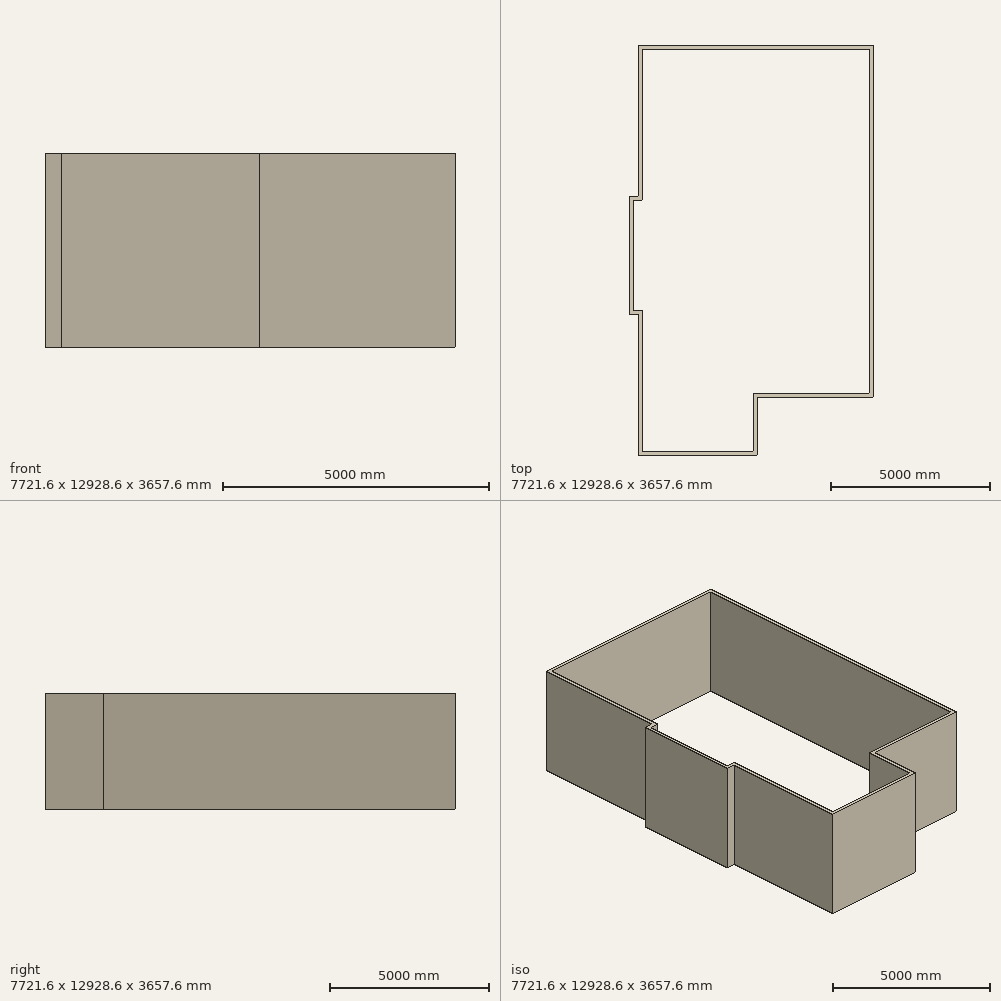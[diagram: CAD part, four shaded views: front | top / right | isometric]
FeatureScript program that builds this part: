
annotation { "Feature Type Name" : "Feature", "Feature Type Description" : "" }
export const myFeature = defineFeature(function(context is Context, id is Id, definition is map)
    precondition{}
    {
        {
            var Q0;
            Q0=qCreatedBy(makeId("Top.planeOp"),FACE);
            var sketch = newSketch(context, id + "F0", { "sketchPlane" : qUnion([Q0])});
            skLineSegment(sketch, "E0", {"start": v(3683, 0) * mm, "end": v(3683, 11099.8) * mm});
            skLineSegment(sketch, "E1", {"start": v(3683, 11099.8) * mm, "end": v(-3733.8, 11099.8) * mm});
            skLineSegment(sketch, "E2", {"start": v(-3733.8, 11099.8) * mm, "end": v(-3733.8, 6324.6) * mm});
            skLineSegment(sketch, "E3", {"start": v(-3733.8, 6324.6) * mm, "end": v(-4038.6, 6324.6) * mm});
            skLineSegment(sketch, "E4", {"start": v(-4038.6, 6324.6) * mm, "end": v(-4038.6, 2616.2) * mm});
            skLineSegment(sketch, "E5", {"start": v(-4038.6, 2616.2) * mm, "end": v(-3733.8, 2616.2) * mm});
            skLineSegment(sketch, "E6", {"start": v(-3733.8, 2616.2) * mm, "end": v(-3733.8, -1828.8) * mm});
            skLineSegment(sketch, "E7", {"start": v(0, -1828.8) * mm, "end": v(0, 0) * mm});
            skLineSegment(sketch, "E8", {"start": v(0, 0) * mm, "end": v(3683, 0) * mm});
            skPoint(sketch, "E9.orphan", {"position": v(3683, 0) * mm});
            skLineSegment(sketch, "E10", {"start": v(-3733.8, -1828.8) * mm, "end": v(0, -1828.8) * mm});
            skLineSegment(sketch, "E11.0", {"start": v(-127, -1701.8) * mm, "end": v(-127, 127) * mm});
            skLineSegment(sketch, "E11.1", {"start": v(-3606.8, -1701.8) * mm, "end": v(-127, -1701.8) * mm});
            skLineSegment(sketch, "E11.2", {"start": v(-3606.8, 2743.2) * mm, "end": v(-3606.8, -1701.8) * mm});
            skLineSegment(sketch, "E11.3", {"start": v(-3911.6, 2743.2) * mm, "end": v(-3606.8, 2743.2) * mm});
            skLineSegment(sketch, "E11.4", {"start": v(-3911.6, 6197.6) * mm, "end": v(-3911.6, 2743.2) * mm});
            skLineSegment(sketch, "E11.5", {"start": v(-127, 127) * mm, "end": v(3556, 127) * mm});
            skLineSegment(sketch, "E11.6", {"start": v(-3606.8, 6197.6) * mm, "end": v(-3911.6, 6197.6) * mm});
            skLineSegment(sketch, "E11.7", {"start": v(-3606.8, 10972.8) * mm, "end": v(-3606.8, 6197.6) * mm});
            skLineSegment(sketch, "E11.8", {"start": v(3556, 10972.8) * mm, "end": v(-3606.8, 10972.8) * mm});
            skLineSegment(sketch, "E11.9", {"start": v(3556, 127) * mm, "end": v(3556, 10972.8) * mm});
            skLineSegment(sketch, "E12.bottom", {"start": v(-3746.5, 438.15) * mm, "end": v(-3594.1, 438.15) * mm, "construction": true});
            skLineSegment(sketch, "E12.top", {"start": v(-3746.5, 1352.55) * mm, "end": v(-3594.1, 1352.55) * mm, "construction": true});
            skLineSegment(sketch, "E12.left", {"start": v(-3746.5, 438.15) * mm, "end": v(-3746.5, 1352.55) * mm, "construction": true});
            skLineSegment(sketch, "E12.right", {"start": v(-3594.1, 438.15) * mm, "end": v(-3594.1, 1352.55) * mm, "construction": true});
            skLineSegment(sketch, "E13", {"start": v(-3606.8, 2609.85) * mm, "end": v(-2933.7, 2609.85) * mm, "construction": true});
            skLineSegment(sketch, "E14", {"start": v(-2933.7, 2609.85) * mm, "end": v(-2933.7, 2743.2) * mm, "construction": true});
            skLineSegment(sketch, "E15", {"start": v(-2933.7, 2743.2) * mm, "end": v(-3606.8, 2743.2) * mm, "construction": true});
            skLineSegment(sketch, "E16.bottom", {"start": v(-2705.1, -1689.1) * mm, "end": v(-1054.1, -1689.1) * mm, "construction": true});
            skLineSegment(sketch, "E16.top", {"start": v(-2705.1, -1841.5) * mm, "end": v(-1054.1, -1841.5) * mm, "construction": true});
            skLineSegment(sketch, "E16.left", {"start": v(-2705.1, -1689.1) * mm, "end": v(-2705.1, -1841.5) * mm, "construction": true});
            skLineSegment(sketch, "E16.right", {"start": v(-1054.1, -1689.1) * mm, "end": v(-1054.1, -1841.5) * mm, "construction": true});
            skLineSegment(sketch, "E17", {"start": v(-127, 127) * mm, "end": v(-127, 2609.85) * mm, "construction": true});
            skLineSegment(sketch, "E18", {"start": v(-127, 2609.85) * mm, "end": v(-800.1, 2609.85) * mm, "construction": true});
            skLineSegment(sketch, "E19", {"start": v(-800.1, 2743.2) * mm, "end": v(-88.9, 2743.2) * mm, "construction": true});
            skLineSegment(sketch, "E20", {"start": v(-88.9, 2743.2) * mm, "end": v(660.4, 3359.05) * mm, "construction": true});
            skLineSegment(sketch, "E21", {"start": v(660.4, 3359.05) * mm, "end": v(660.4, 5268.85) * mm, "construction": true});
            skLineSegment(sketch, "E22", {"start": v(0, 127) * mm, "end": v(0, 2680.36) * mm, "construction": true});
            skLineSegment(sketch, "E23", {"start": v(76.33, 2747.5) * mm, "end": v(800.1, 1866.9) * mm, "construction": true});
            skLineSegment(sketch, "E24", {"start": v(800.1, 1866.9) * mm, "end": v(800.1, 127) * mm, "construction": true});
            skLineSegment(sketch, "E25", {"start": v(-800.1, 2743.2) * mm, "end": v(-800.1, 2609.85) * mm});
            skLineSegment(sketch, "E26", {"start": v(76.33, 2747.5) * mm, "end": v(812.8, 3352.8) * mm, "construction": true});
            skLineSegment(sketch, "E27", {"start": v(812.8, 3352.8) * mm, "end": v(3556, 3352.8) * mm, "construction": true});
            skLineSegment(sketch, "E28", {"start": v(3556, 3479.8) * mm, "end": v(787.4, 3479.8) * mm, "construction": true});
            skLineSegment(sketch, "E29", {"start": v(787.4, 3479.8) * mm, "end": v(787.4, 5181.6) * mm, "construction": true});
            skLineSegment(sketch, "E30", {"start": v(787.4, 5181.6) * mm, "end": v(3556, 5181.6) * mm, "construction": true});
            skLineSegment(sketch, "E31", {"start": v(3541.89, 5308.6) * mm, "end": v(781.97, 5308.6) * mm, "construction": true});
            skLineSegment(sketch, "E32", {"start": v(781.97, 5308.6) * mm, "end": v(0, 5845.85) * mm, "construction": true});
            skLineSegment(sketch, "E33", {"start": v(0, 8534.4) * mm, "end": v(698.5, 8534.4) * mm, "construction": true});
            skLineSegment(sketch, "E34", {"start": v(660.4, 5268.85) * mm, "end": v(-293.97, 5924.55) * mm, "construction": true});
            skLineSegment(sketch, "E35", {"start": v(-293.97, 5924.55) * mm, "end": v(-293.97, 6197.6) * mm, "construction": true});
            skLineSegment(sketch, "E36", {"start": v(-293.97, 6197.6) * mm, "end": v(-3606.8, 6197.6) * mm, "construction": true});
            skLineSegment(sketch, "E37.bottom", {"start": v(1346.2, 139.7) * mm, "end": v(2070.1, 139.7) * mm, "construction": true});
            skLineSegment(sketch, "E37.top", {"start": v(1346.2, -12.7) * mm, "end": v(2070.1, -12.7) * mm, "construction": true});
            skLineSegment(sketch, "E37.left", {"start": v(1346.2, 139.7) * mm, "end": v(1346.2, -12.7) * mm, "construction": true});
            skLineSegment(sketch, "E37.right", {"start": v(2070.1, 139.7) * mm, "end": v(2070.1, -12.7) * mm, "construction": true});
            skLineSegment(sketch, "E38.bottom", {"start": v(3543.3, 2781.3) * mm, "end": v(3695.7, 2781.3) * mm, "construction": true});
            skLineSegment(sketch, "E38.top", {"start": v(3543.3, 2051.05) * mm, "end": v(3695.7, 2051.05) * mm, "construction": true});
            skLineSegment(sketch, "E38.left", {"start": v(3543.3, 2781.3) * mm, "end": v(3543.3, 2051.05) * mm, "construction": true});
            skLineSegment(sketch, "E38.right", {"start": v(3695.7, 2781.3) * mm, "end": v(3695.7, 2051.05) * mm, "construction": true});
            skLineSegment(sketch, "E39", {"start": v(0, 2680.36) * mm, "end": v(698.5, 1830.5) * mm, "construction": true});
            skLineSegment(sketch, "E40", {"start": v(698.5, 1830.5) * mm, "end": v(698.5, 127) * mm, "construction": true});
            skLineSegment(sketch, "E41.bottom", {"start": v(3543.3, 4610.1) * mm, "end": v(3695.7, 4610.1) * mm, "construction": true});
            skLineSegment(sketch, "E41.top", {"start": v(3543.3, 4038.6) * mm, "end": v(3695.7, 4038.6) * mm, "construction": true});
            skLineSegment(sketch, "E41.left", {"start": v(3543.3, 4610.1) * mm, "end": v(3543.3, 4038.6) * mm, "construction": true});
            skLineSegment(sketch, "E41.right", {"start": v(3695.7, 4610.1) * mm, "end": v(3695.7, 4038.6) * mm, "construction": true});
            skLineSegment(sketch, "E42.bottom", {"start": v(635, 4394.2) * mm, "end": v(787.4, 4394.2) * mm, "construction": true});
            skLineSegment(sketch, "E42.top", {"start": v(635, 3632.2) * mm, "end": v(787.4, 3632.2) * mm, "construction": true});
            skLineSegment(sketch, "E42.left", {"start": v(635, 4394.2) * mm, "end": v(635, 3632.2) * mm, "construction": true});
            skLineSegment(sketch, "E42.right", {"start": v(787.4, 4394.2) * mm, "end": v(787.4, 3632.2) * mm, "construction": true});
            skLineSegment(sketch, "E43.bottom", {"start": v(-427.32, 6172.2) * mm, "end": v(-1189.32, 6172.2) * mm, "construction": true});
            skLineSegment(sketch, "E43.top", {"start": v(-427.32, 6324.6) * mm, "end": v(-1189.32, 6324.6) * mm, "construction": true});
            skLineSegment(sketch, "E43.left", {"start": v(-427.32, 6172.2) * mm, "end": v(-427.32, 6324.6) * mm, "construction": true});
            skLineSegment(sketch, "E43.right", {"start": v(-1189.32, 6172.2) * mm, "end": v(-1189.32, 6324.6) * mm, "construction": true});
            skLineSegment(sketch, "E44.bottom", {"start": v(-4064, 3619.5) * mm, "end": v(-3911.6, 3619.5) * mm, "construction": true});
            skLineSegment(sketch, "E44.top", {"start": v(-4064, 4349.75) * mm, "end": v(-3911.6, 4349.75) * mm, "construction": true});
            skLineSegment(sketch, "E44.left", {"start": v(-4064, 3619.5) * mm, "end": v(-4064, 4349.75) * mm, "construction": true});
            skLineSegment(sketch, "E44.right", {"start": v(-3911.6, 3619.5) * mm, "end": v(-3911.6, 4349.75) * mm, "construction": true});
            skLineSegment(sketch, "E45.bottom", {"start": v(3543.3, 5867.4) * mm, "end": v(3695.7, 5867.4) * mm, "construction": true});
            skLineSegment(sketch, "E45.top", {"start": v(3543.3, 7061.2) * mm, "end": v(3695.7, 7061.2) * mm, "construction": true});
            skLineSegment(sketch, "E45.left", {"start": v(3543.3, 5867.4) * mm, "end": v(3543.3, 7061.2) * mm, "construction": true});
            skLineSegment(sketch, "E45.right", {"start": v(3695.7, 5867.4) * mm, "end": v(3695.7, 7061.2) * mm, "construction": true});
            skLineSegment(sketch, "E46.bottom", {"start": v(3543.3, 9438.28) * mm, "end": v(3695.7, 9438.28) * mm, "construction": true});
            skLineSegment(sketch, "E46.top", {"start": v(3543.3, 10256.66) * mm, "end": v(3695.7, 10256.66) * mm, "construction": true});
            skLineSegment(sketch, "E46.left", {"start": v(3543.3, 9438.28) * mm, "end": v(3543.3, 10256.66) * mm, "construction": true});
            skLineSegment(sketch, "E46.right", {"start": v(3695.7, 9438.28) * mm, "end": v(3695.7, 10256.66) * mm, "construction": true});
            skLineSegment(sketch, "E47.bottom", {"start": v(2881.46, 10778.72) * mm, "end": v(1984.95, 10778.72) * mm, "construction": true});
            skLineSegment(sketch, "E47.top", {"start": v(2881.46, 10931.12) * mm, "end": v(1984.95, 10931.12) * mm, "construction": true});
            skLineSegment(sketch, "E47.left", {"start": v(2881.46, 10778.72) * mm, "end": v(2881.46, 10931.12) * mm, "construction": true});
            skLineSegment(sketch, "E47.right", {"start": v(1984.95, 10778.72) * mm, "end": v(1984.95, 10931.12) * mm, "construction": true});
            skLineSegment(sketch, "E48.bottom", {"start": v(1766.71, 10778.72) * mm, "end": v(966.52, 10778.72) * mm, "construction": true});
            skLineSegment(sketch, "E48.top", {"start": v(1766.71, 10931.12) * mm, "end": v(966.52, 10931.12) * mm, "construction": true});
            skLineSegment(sketch, "E48.left", {"start": v(1766.71, 10778.72) * mm, "end": v(1766.71, 10931.12) * mm, "construction": true});
            skLineSegment(sketch, "E48.right", {"start": v(966.52, 10778.72) * mm, "end": v(966.52, 10931.12) * mm, "construction": true});
            skLineSegment(sketch, "E49.bottom", {"start": v(-1415.88, 10778.72) * mm, "end": v(-2525.25, 10778.72) * mm, "construction": true});
            skLineSegment(sketch, "E49.top", {"start": v(-1415.88, 10931.12) * mm, "end": v(-2525.25, 10931.12) * mm, "construction": true});
            skLineSegment(sketch, "E49.left", {"start": v(-1415.88, 10778.72) * mm, "end": v(-1415.88, 10931.12) * mm, "construction": true});
            skLineSegment(sketch, "E49.right", {"start": v(-2525.25, 10778.72) * mm, "end": v(-2525.25, 10931.12) * mm, "construction": true});
            skPoint(sketch, "E50.oppositeSnap0", {"position": v(-3606.8, 8585.2) * mm});
            skLineSegment(sketch, "E50.bottom", {"start": v(-3936.87, 7828.6) * mm, "end": v(-4089.27, 7828.6) * mm, "construction": true});
            skLineSegment(sketch, "E50.top", {"start": v(-3936.87, 8585.2) * mm, "end": v(-4089.27, 8585.2) * mm, "construction": true});
            skLineSegment(sketch, "E50.left", {"start": v(-3936.87, 7828.6) * mm, "end": v(-3936.87, 8585.2) * mm, "construction": true});
            skLineSegment(sketch, "E50.right", {"start": v(-4089.27, 7828.6) * mm, "end": v(-4089.27, 8585.2) * mm, "construction": true});
            skLineSegment(sketch, "E51", {"start": v(-3606.8, 6299.2) * mm, "end": v(-293.97, 6299.2) * mm, "construction": true});
            skLineSegment(sketch, "E52", {"start": v(-293.97, 6299.2) * mm, "end": v(-293.97, 9093.2) * mm, "construction": true});
            skLineSegment(sketch, "E53", {"start": v(-293.97, 9093.2) * mm, "end": v(-805.07, 9093.2) * mm, "construction": true});
            skLineSegment(sketch, "E54", {"start": v(-805.07, 9093.2) * mm, "end": v(-805.07, 9245.6) * mm, "construction": true});
            skLineSegment(sketch, "E55", {"start": v(-805.07, 9245.6) * mm, "end": v(-293.97, 9245.6) * mm, "construction": true});
            skLineSegment(sketch, "E56", {"start": v(-293.97, 9245.6) * mm, "end": v(-293.97, 10972.8) * mm, "construction": true});
            skLineSegment(sketch, "E57", {"start": v(-107.65, 5765.72) * mm, "end": v(520.4, 5334.22) * mm, "construction": true});
            skLineSegment(sketch, "E58", {"start": v(520.4, 5334.22) * mm, "end": v(606.7, 5459.83) * mm, "construction": true});
            skLineSegment(sketch, "E59", {"start": v(606.7, 5459.83) * mm, "end": v(-21.35, 5891.33) * mm, "construction": true});
            skLineSegment(sketch, "E60", {"start": v(-21.35, 5891.33) * mm, "end": v(-107.65, 5765.72) * mm, "construction": true});
            skLineSegment(sketch, "E61", {"start": v(50.34, 2893.8) * mm, "end": v(639.02, 3377.65) * mm, "construction": true});
            skLineSegment(sketch, "E62", {"start": v(639.02, 3377.65) * mm, "end": v(735.79, 3259.91) * mm, "construction": true});
            skLineSegment(sketch, "E63", {"start": v(735.79, 3259.91) * mm, "end": v(147.1, 2776.07) * mm, "construction": true});
            skLineSegment(sketch, "E64", {"start": v(147.1, 2776.07) * mm, "end": v(50.34, 2893.8) * mm, "construction": true});
            skLineSegment(sketch, "E65", {"start": v(800.1, 8534.4) * mm, "end": v(800.1, 7010.4) * mm, "construction": true});
            skLineSegment(sketch, "E66", {"start": v(800.1, 7010.4) * mm, "end": v(0, 5845.85) * mm, "construction": true});
            skLineSegment(sketch, "E67", {"start": v(0, 6025.27) * mm, "end": v(698.5, 7041.94) * mm, "construction": true});
            skLineSegment(sketch, "E68", {"start": v(698.5, 7041.94) * mm, "end": v(698.5, 8534.4) * mm, "construction": true});
            skLineSegment(sketch, "E69.bottom", {"start": v(-4064, 4527.55) * mm, "end": v(-3911.6, 4527.55) * mm, "construction": true});
            skLineSegment(sketch, "E69.top", {"start": v(-4064, 5257.8) * mm, "end": v(-3911.6, 5257.8) * mm, "construction": true});
            skLineSegment(sketch, "E69.left", {"start": v(-4064, 4527.55) * mm, "end": v(-4064, 5257.8) * mm, "construction": true});
            skLineSegment(sketch, "E69.right", {"start": v(-3911.6, 4527.55) * mm, "end": v(-3911.6, 5257.8) * mm, "construction": true});
            skLineSegment(sketch, "E70.trimOffspring", {"start": v(800.1, 8534.4) * mm, "end": v(3556, 8534.4) * mm, "construction": true});
            skLineSegment(sketch, "E71", {"start": v(0, 8686.8) * mm, "end": v(3556, 8686.8) * mm, "construction": true});
            skLineSegment(sketch, "E72.trimOffspring", {"start": v(0, 6025.27) * mm, "end": v(0, 8534.4) * mm, "construction": true});
            skLineSegment(sketch, "E73.trimOffspring", {"start": v(0, 8686.8) * mm, "end": v(0, 10972.8) * mm, "construction": true});
            skSolve(sketch);
        }
        {
            var Q0;
            Q0=qSketchRegion(id+"F0",true);
            extrude(context, id + "F1", {"entities" : qUnion([Q0]), "depth" : 3657.6 * mm});
        }
    });
